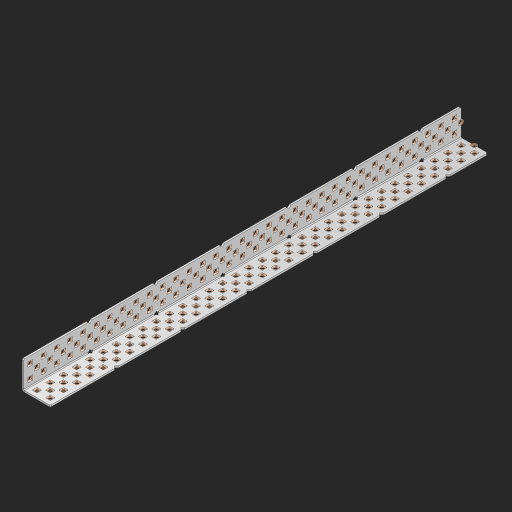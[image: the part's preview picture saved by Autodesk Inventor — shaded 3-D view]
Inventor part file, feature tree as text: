
AUTODESK INVENTOR PART (.ipt)
format: ipt  version: 2023 (Build 270158000, 158)  size: 2,248,704 bytes
history: native  units: in
note: dims shown in document units (in); Inventor stores cm internally (conversion verified against a paired STEP export)
features: other x204, extrude x196, sheet_metal_op x8, sketch x7, pattern_linear x2, mirror x1, chamfer x1
ambient origin geometry x8: Origin, YZ Plane, XZ Plane, XY Plane, X Axis, Y Axis, Z Axis, Center Point
bodies: Solid1 (feature_tree), Body (feature_tree)
feature tree (419):
  sheet_metal_op  "Flanges"
  sheet_metal_op  "Body Pattern"
  pattern_linear  "Center Pattern"  Spacing1=1.0in  [1 undecoded]
  other  "Arc Length"
  pattern_linear  "Notch Pattern"  Spacing1=0.25in  [1 undecoded]
  other  "Diagonal Plane"
  mirror  "Everything Mirrored"
  chamfer  "End Chamfer"
  sketch  "Sketch1"  dims[d0=1.0in]
  other  "Plate1"
  sketch  "Sketch2"  dims[d1=16.5in]
  other  "Plate2"
  sheet_metal_op  "Bend1"
  sheet_metal_op  "Corner1"
  sketch  "Sketch8"  dims[d2=0.0625in]
  sketch  "Sketch9"  dims[d3=0.0625in]
  other  "Srf91"
  sheet_metal_op  "Body Pattern Sketch"
  other  "Srf92"
  sketch  "Sketch13"  dims[d4=0.0312in]
  sketch  "Sketch15"  dims[d5=0.125in]
  sketch  "Sketch16"  dims[d6=0.0625in d7=1.0in d8=90.0deg d9=0.0312in d10=0.25in d11=0.0625in d12=0.0625in d49=0.182in d50=0.02in d52=0.25in d53=0.0625in d54=0.0in d55=0.172in d56=1.0in d57=0.0in d60=12.9921in d62=0.5in d63=0.7874in d65=0.5in d85=0.1473in d86=0.1782in d89=0.0625in d90=0.0in d91=0.04in d92=0.0491in d95=2.5in d96=0.04in d97=0.25in d98=45.0deg d99=0.25in d106=0.182in d107=0.02in d108=0.5in d110=0.0625in d111=0.0in d112=0.172in d113=0.5in d114=0.0in d117=0.5in d123=0.25in d125=0.25in d126=0.0491in d127=0.1473in d128=0.08in d129=0.04in d130=2.5in]
  other  "Srf786"
  other  "Srf856"
  other  "Srf857"
  other  "Srf858"
  other  "Srf859"
  other  "Srf860"
  other  "Srf861"
  other  "Srf889"
  other  "Srf890"
  other  "Srf891"
  other  "Srf1275"
  other  "Srf1276"
  other  "Srf1278"
  other  "Srf1279"
  other  "Srf1280"
  other  "Srf1281"
  other  "Srf1282"
  other  "Srf1283"
  other  "Srf1277"
  other  "Srf1285"
  other  "Srf1286"
  other  "Srf1287"
  other  "Srf1383"
  other  "Srf1384"
  other  "Srf1385"
  other  "Srf1386"
  other  "Srf1387"
  other  "Srf1388"
  other  "Srf1389"
  other  "Srf1390"
  other  "Srf1391"
  other  "Srf1392"
  other  "Srf1393"
  other  "Srf1394"
  other  "Srf1395"
  other  "Srf1396"
  other  "Srf1397"
  other  "Srf1398"
  other  "Srf1399"
  other  "Srf1400"
  other  "Srf1401"
  other  "Srf1402"
  other  "Srf1403"
  other  "Srf1404"
  other  "Srf1405"
  other  "Srf1406"
  other  "Srf1407"
  other  "Srf1408"
  other  "Srf1409"
  other  "Srf1410"
  other  "Srf1411"
  other  "Srf1412"
  other  "Srf1413"
  other  "Srf1414"
  other  "Srf1415"
  other  "Srf1416"
  other  "Srf1417"
  other  "Srf1418"
  other  "Srf1419"
  other  "Srf1420"
  other  "Srf1421"
  other  "Srf1422"
  other  "Srf1423"
  other  "Srf1424"
  other  "Srf1425"
  other  "Srf1426"
  other  "Srf1427"
  other  "Srf1428"
  other  "Srf1429"
  other  "Srf1430"
  other  "Srf1431"
  other  "Srf1432"
  other  "Srf1433"
  other  "Srf1434"
  other  "Srf1435"
  other  "Srf1436"
  other  "Srf1437"
  other  "Srf1438"
  other  "Srf1439"
  other  "Srf1440"
  other  "Srf1445"
  other  "Srf1446"
  other  "Srf1447"
  other  "Srf1448"
  other  "Srf1449"
  other  "Srf1450"
  other  "Srf1451"
  other  "Srf1452"
  other  "Srf1453"
  other  "Srf1454"
  other  "Srf1455"
  other  "Srf1456"
  other  "Srf1457"
  other  "Srf1458"
  other  "Srf1459"
  other  "Srf1460"
  other  "Srf1461"
  other  "Srf1462"
  other  "Srf1463"
  other  "Srf1464"
  other  "Srf1465"
  other  "Srf1466"
  other  "Srf1467"
  other  "Srf1468"
  other  "Srf1469"
  other  "Srf1470"
  other  "Srf1471"
  other  "Srf1472"
  other  "Srf1473"
  other  "Srf1475"
  other  "Srf1476"
  other  "Srf1477"
  other  "Srf1478"
  other  "Srf1479"
  other  "Srf1480"
  other  "Srf1481"
  other  "Srf1482"
  other  "Srf1483"
  other  "Srf1484"
  other  "Srf1485"
  other  "Srf1486"
  other  "Srf1487"
  other  "Srf1488"
  other  "Srf1489"
  other  "Srf1490"
  other  "Srf1491"
  other  "Srf1492"
  other  "Srf1493"
  other  "Srf1494"
  other  "Srf1495"
  other  "Srf1496"
  other  "Srf1497"
  other  "Srf1498"
  other  "Srf1499"
  other  "Srf1500"
  other  "Srf1501"
  other  "Srf1502"
  other  "Srf1503"
  other  "Srf1504"
  other  "Srf1505"
  other  "Srf1506"
  other  "Srf1507"
  other  "Srf1508"
  other  "Srf1509"
  other  "Srf1510"
  other  "Srf1511"
  other  "Srf1512"
  other  "Srf1513"
  other  "Srf1514"
  other  "Srf1515"
  other  "Srf1516"
  other  "Srf1517"
  other  "Srf1518"
  other  "Srf1519"
  other  "Srf1520"
  other  "Srf1521"
  other  "Srf1522"
  other  "Srf1523"
  other  "Srf1524"
  other  "Srf1525"
  other  "Srf1526"
  other  "Srf1527"
  other  "Srf1528"
  other  "Srf1529"
  other  "Srf1530"
  other  "Srf1531"
  other  "Srf1532"
  other  "Srf1537"
  other  "Srf1538"
  other  "Srf1539"
  other  "Srf1540"
  other  "Srf1541"
  other  "Srf1542"
  other  "Srf1543"
  other  "Srf1544"
  other  "Srf1545"
  other  "Srf1546"
  other  "Srf1547"
  other  "Srf1548"
  other  "Srf1549"
  other  "Srf1550"
  other  "Srf1551"
  other  "Srf1552"
  other  "Srf1553"
  other  "Srf1554"
  other  "Srf1555"
  other  "Srf1556"
  other  "Srf1557"
  other  "Srf1558"
  other  "Srf1559"
  other  "Srf1560"
  other  "Srf1561"
  other  "Srf1562"
  other  "Srf1563"
  other  "Srf1564"
  other  "Srf1565"
  sheet_metal_op  "Body Stamp"
  sheet_metal_op  "Body Circle"
  other  "Center Stamp"
  other  "Center Circle"
  sheet_metal_op  "Notch"
  extrude  "ExtrusionSrf92"  Depth=0.0625in
  extrude  "ExtrusionSrf856"  Depth=0.0625in
  extrude  "ExtrusionSrf857"  Depth=0.182in
  extrude  "ExtrusionSrf858"  Depth=0.02in
  extrude  "ExtrusionSrf859"  Depth=0.25in
  extrude  "ExtrusionSrf860"  Depth=0.0625in
  extrude  "ExtrusionSrf861"  TaperAngle=0.0deg  [1 undecoded]
  extrude  "ExtrusionSrf889"  Depth=2.5in
  extrude  "ExtrusionSrf890"  Depth=1.0in TaperAngle=0.0deg
  extrude  "ExtrusionSrf891"  Depth=2.5in
  extrude  "ExtrusionSrf1275"  Depth=0.5in
  extrude  "ExtrusionSrf1276"  Depth=2.5in
  extrude  "ExtrusionSrf1277"  Depth=2.5in
  extrude  "ExtrusionSrf1278"  Depth=0.0625in
  extrude  "ExtrusionSrf1279"  Depth=2.5in TaperAngle=0.0deg
  extrude  "ExtrusionSrf1280"  Depth=2.5in
  extrude  "ExtrusionSrf1281"  Depth=0.25in TaperAngle=45.0deg
  extrude  "ExtrusionSrf1282"  Depth=0.25in
  extrude  "ExtrusionSrf1345"  Depth=0.182in
  extrude  "ExtrusionSrf1346"  Depth=0.02in
  extrude  "ExtrusionSrf1347"  Depth=0.5in
  extrude  "ExtrusionSrf1348"  Depth=0.0625in
  extrude  "ExtrusionSrf1383"  TaperAngle=0.0deg  [1 undecoded]
  extrude  "ExtrusionSrf1384"  Depth=2.5in
  extrude  "ExtrusionSrf1385"  Depth=0.5in TaperAngle=0.0deg
  extrude  "ExtrusionSrf1386"  Depth=0.5in
  extrude  "ExtrusionSrf1387"  Depth=0.25in
  extrude  "ExtrusionSrf1388"  Depth=0.25in
  extrude  "ExtrusionSrf1389"  Depth=2.5in
  extrude  "ExtrusionSrf1390"  Depth=2.5in
  extrude  "ExtrusionSrf1391"  Depth=2.5in
  extrude  "ExtrusionSrf1392"  Depth=2.5in
  extrude  "ExtrusionSrf1393"  Depth=2.5in
  extrude  "ExtrusionSrf1394"  [1 undecoded]
  extrude  "ExtrusionSrf1395"  [1 undecoded]
  extrude  "ExtrusionSrf1396"  [1 undecoded]
  extrude  "ExtrusionSrf1397"  [1 undecoded]
  extrude  "ExtrusionSrf1398"  [1 undecoded]
  extrude  "ExtrusionSrf1399"  [1 undecoded]
  extrude  "ExtrusionSrf1400"  [1 undecoded]
  extrude  "ExtrusionSrf1401"  [1 undecoded]
  extrude  "ExtrusionSrf1402"  [1 undecoded]
  extrude  "ExtrusionSrf1403"  [1 undecoded]
  extrude  "ExtrusionSrf1404"  [1 undecoded]
  extrude  "ExtrusionSrf1405"  [1 undecoded]
  extrude  "ExtrusionSrf1406"  [1 undecoded]
  extrude  "ExtrusionSrf1407"  [1 undecoded]
  extrude  "ExtrusionSrf1408"  [1 undecoded]
  extrude  "ExtrusionSrf1409"  [1 undecoded]
  extrude  "ExtrusionSrf1410"  [1 undecoded]
  extrude  "ExtrusionSrf1411"  [1 undecoded]
  extrude  "ExtrusionSrf1412"  [1 undecoded]
  extrude  "ExtrusionSrf1413"  [1 undecoded]
  extrude  "ExtrusionSrf1414"  [1 undecoded]
  extrude  "ExtrusionSrf1415"  [1 undecoded]
  extrude  "ExtrusionSrf1416"  [1 undecoded]
  extrude  "ExtrusionSrf1417"  [1 undecoded]
  extrude  "ExtrusionSrf1418"  [1 undecoded]
  extrude  "ExtrusionSrf1419"  [1 undecoded]
  extrude  "ExtrusionSrf1420"  [1 undecoded]
  extrude  "ExtrusionSrf1421"  [1 undecoded]
  extrude  "ExtrusionSrf1422"  [1 undecoded]
  extrude  "ExtrusionSrf1423"  [1 undecoded]
  extrude  "ExtrusionSrf1424"  [1 undecoded]
  extrude  "ExtrusionSrf1425"  [1 undecoded]
  extrude  "ExtrusionSrf1426"  [1 undecoded]
  extrude  "ExtrusionSrf1427"  [1 undecoded]
  extrude  "ExtrusionSrf1428"  [1 undecoded]
  extrude  "ExtrusionSrf1429"  [1 undecoded]
  extrude  "ExtrusionSrf1430"  [1 undecoded]
  extrude  "ExtrusionSrf1431"  [1 undecoded]
  extrude  "ExtrusionSrf1432"  [1 undecoded]
  extrude  "ExtrusionSrf1433"  [1 undecoded]
  extrude  "ExtrusionSrf1434"  [1 undecoded]
  extrude  "ExtrusionSrf1435"  [1 undecoded]
  extrude  "ExtrusionSrf1436"  [1 undecoded]
  extrude  "ExtrusionSrf1437"  [1 undecoded]
  extrude  "ExtrusionSrf1438"  [1 undecoded]
  extrude  "ExtrusionSrf1439"  [1 undecoded]
  extrude  "ExtrusionSrf1440"  [1 undecoded]
  extrude  "ExtrusionSrf1445"  [1 undecoded]
  extrude  "ExtrusionSrf1446"  [1 undecoded]
  extrude  "ExtrusionSrf1447"  [1 undecoded]
  extrude  "ExtrusionSrf1448"  [1 undecoded]
  extrude  "ExtrusionSrf1449"  [1 undecoded]
  extrude  "ExtrusionSrf1450"  [1 undecoded]
  extrude  "ExtrusionSrf1451"  [1 undecoded]
  extrude  "ExtrusionSrf1452"  [1 undecoded]
  extrude  "ExtrusionSrf1453"  [1 undecoded]
  extrude  "ExtrusionSrf1454"  [1 undecoded]
  extrude  "ExtrusionSrf1455"  [1 undecoded]
  extrude  "ExtrusionSrf1456"  [1 undecoded]
  extrude  "ExtrusionSrf1457"  [1 undecoded]
  extrude  "ExtrusionSrf1458"  [1 undecoded]
  extrude  "ExtrusionSrf1459"  [1 undecoded]
  extrude  "ExtrusionSrf1460"  [1 undecoded]
  extrude  "ExtrusionSrf1461"  [1 undecoded]
  extrude  "ExtrusionSrf1462"  [1 undecoded]
  extrude  "ExtrusionSrf1463"  [1 undecoded]
  extrude  "ExtrusionSrf1464"  [1 undecoded]
  extrude  "ExtrusionSrf1465"  [1 undecoded]
  extrude  "ExtrusionSrf1466"  [1 undecoded]
  extrude  "ExtrusionSrf1467"  [1 undecoded]
  extrude  "ExtrusionSrf1468"  [1 undecoded]
  extrude  "ExtrusionSrf1469"  [1 undecoded]
  extrude  "ExtrusionSrf1470"  [1 undecoded]
  extrude  "ExtrusionSrf1471"  [1 undecoded]
  extrude  "ExtrusionSrf1472"  [1 undecoded]
  extrude  "ExtrusionSrf1473"  [1 undecoded]
  extrude  "ExtrusionSrf1475"  [1 undecoded]
  extrude  "ExtrusionSrf1476"  [1 undecoded]
  extrude  "ExtrusionSrf1477"  [1 undecoded]
  extrude  "ExtrusionSrf1478"  [1 undecoded]
  extrude  "ExtrusionSrf1479"  [1 undecoded]
  extrude  "ExtrusionSrf1480"  [1 undecoded]
  extrude  "ExtrusionSrf1481"  [1 undecoded]
  extrude  "ExtrusionSrf1482"  [1 undecoded]
  extrude  "ExtrusionSrf1483"  [1 undecoded]
  extrude  "ExtrusionSrf1484"  [1 undecoded]
  extrude  "ExtrusionSrf1485"  [1 undecoded]
  extrude  "ExtrusionSrf1486"  [1 undecoded]
  extrude  "ExtrusionSrf1487"  [1 undecoded]
  extrude  "ExtrusionSrf1488"  [1 undecoded]
  extrude  "ExtrusionSrf1489"  [1 undecoded]
  extrude  "ExtrusionSrf1490"  [1 undecoded]
  extrude  "ExtrusionSrf1491"  [1 undecoded]
  extrude  "ExtrusionSrf1492"  [1 undecoded]
  extrude  "ExtrusionSrf1493"  [1 undecoded]
  extrude  "ExtrusionSrf1494"  [1 undecoded]
  extrude  "ExtrusionSrf1495"  [1 undecoded]
  extrude  "ExtrusionSrf1496"  [1 undecoded]
  extrude  "ExtrusionSrf1497"  [1 undecoded]
  extrude  "ExtrusionSrf1498"  [1 undecoded]
  extrude  "ExtrusionSrf1499"  [1 undecoded]
  extrude  "ExtrusionSrf1500"  [1 undecoded]
  extrude  "ExtrusionSrf1501"  [1 undecoded]
  extrude  "ExtrusionSrf1502"  [1 undecoded]
  extrude  "ExtrusionSrf1503"  [1 undecoded]
  extrude  "ExtrusionSrf1504"  [1 undecoded]
  extrude  "ExtrusionSrf1505"  [1 undecoded]
  extrude  "ExtrusionSrf1506"  [1 undecoded]
  extrude  "ExtrusionSrf1507"  [1 undecoded]
  extrude  "ExtrusionSrf1508"  [1 undecoded]
  extrude  "ExtrusionSrf1509"  [1 undecoded]
  extrude  "ExtrusionSrf1510"  [1 undecoded]
  extrude  "ExtrusionSrf1511"  [1 undecoded]
  extrude  "ExtrusionSrf1512"  [1 undecoded]
  extrude  "ExtrusionSrf1513"  [1 undecoded]
  extrude  "ExtrusionSrf1514"  [1 undecoded]
  extrude  "ExtrusionSrf1515"  [1 undecoded]
  extrude  "ExtrusionSrf1516"  [1 undecoded]
  extrude  "ExtrusionSrf1517"  [1 undecoded]
  extrude  "ExtrusionSrf1518"  [1 undecoded]
  extrude  "ExtrusionSrf1519"  [1 undecoded]
  extrude  "ExtrusionSrf1520"  [1 undecoded]
  extrude  "ExtrusionSrf1521"  [1 undecoded]
  extrude  "ExtrusionSrf1522"  [1 undecoded]
  extrude  "ExtrusionSrf1523"  [1 undecoded]
  extrude  "ExtrusionSrf1524"  [1 undecoded]
  extrude  "ExtrusionSrf1525"  [1 undecoded]
  extrude  "ExtrusionSrf1526"  [1 undecoded]
  extrude  "ExtrusionSrf1527"  [1 undecoded]
  extrude  "ExtrusionSrf1528"  [1 undecoded]
  extrude  "ExtrusionSrf1529"  [1 undecoded]
  extrude  "ExtrusionSrf1530"  [1 undecoded]
  extrude  "ExtrusionSrf1531"  [1 undecoded]
  extrude  "ExtrusionSrf1532"  [1 undecoded]
  extrude  "ExtrusionSrf1537"  [1 undecoded]
  extrude  "ExtrusionSrf1538"  [1 undecoded]
  extrude  "ExtrusionSrf1539"  [1 undecoded]
  extrude  "ExtrusionSrf1540"  [1 undecoded]
  extrude  "ExtrusionSrf1541"  [1 undecoded]
  extrude  "ExtrusionSrf1542"  [1 undecoded]
  extrude  "ExtrusionSrf1543"  [1 undecoded]
  extrude  "ExtrusionSrf1544"  [1 undecoded]
  extrude  "ExtrusionSrf1545"  [1 undecoded]
  extrude  "ExtrusionSrf1546"  [1 undecoded]
  extrude  "ExtrusionSrf1547"  [1 undecoded]
  extrude  "ExtrusionSrf1548"  [1 undecoded]
  extrude  "ExtrusionSrf1549"  [1 undecoded]
  extrude  "ExtrusionSrf1550"  [1 undecoded]
  extrude  "ExtrusionSrf1551"  [1 undecoded]
  extrude  "ExtrusionSrf1552"  [1 undecoded]
  extrude  "ExtrusionSrf1553"  [1 undecoded]
  extrude  "ExtrusionSrf1554"  [1 undecoded]
  extrude  "ExtrusionSrf1555"  [1 undecoded]
  extrude  "ExtrusionSrf1556"  [1 undecoded]
  extrude  "ExtrusionSrf1557"  [1 undecoded]
  extrude  "ExtrusionSrf1558"  [1 undecoded]
  extrude  "ExtrusionSrf1559"  [1 undecoded]
  extrude  "ExtrusionSrf1560"  [1 undecoded]
  extrude  "ExtrusionSrf1561"  [1 undecoded]
  extrude  "ExtrusionSrf1562"  [1 undecoded]
  extrude  "ExtrusionSrf1563"  [1 undecoded]
  extrude  "ExtrusionSrf1564"  [1 undecoded]
  extrude  "ExtrusionSrf1565"  [1 undecoded]
note: 167 required parameter values undecoded (feature->parameter linkage not recoverable at this tier; creation-order binding heuristic only, values carry confidence <= 0.55)
